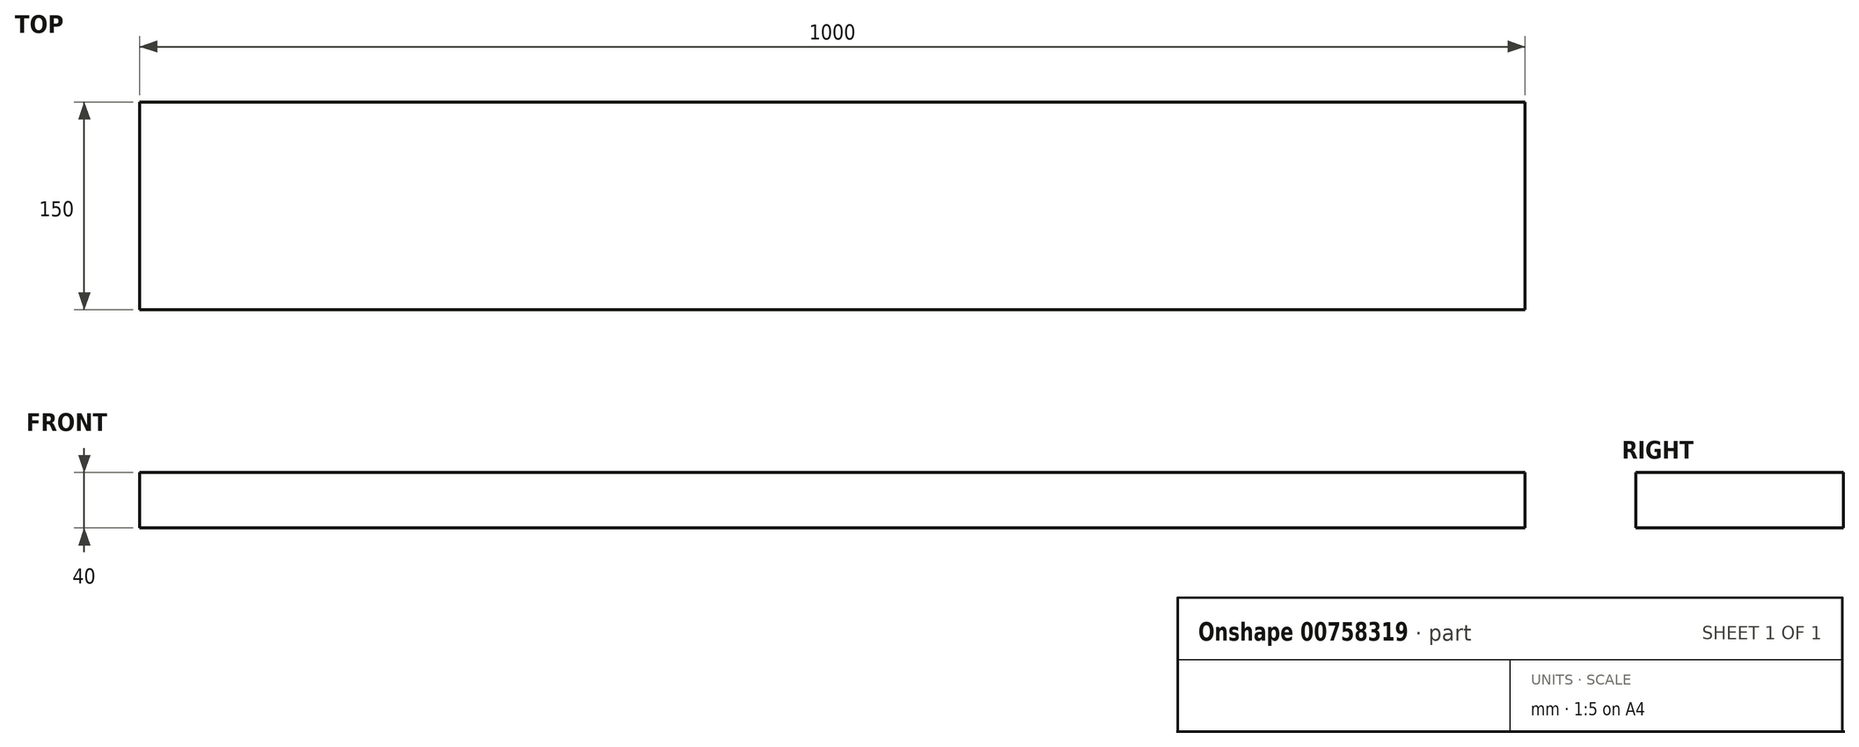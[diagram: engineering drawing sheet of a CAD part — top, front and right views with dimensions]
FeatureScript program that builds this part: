
annotation { "Feature Type Name" : "Feature", "Feature Type Description" : "" }
export const myFeature = defineFeature(function(context is Context, id is Id, definition is map)
    precondition{}
    {
        {
            var Q0;
            Q0=qCreatedBy(makeId("Top.planeOp"),FACE);
            var sketch = newSketch(context, id + "F0", { "sketchPlane" : qUnion([Q0])});
            skLineSegment(sketch, "E0.bottom", {"start": v(0, 0) * mm, "end": v(1000, 0) * mm});
            skLineSegment(sketch, "E0.top", {"start": v(0, 150) * mm, "end": v(1000, 150) * mm});
            skLineSegment(sketch, "E0.left", {"start": v(0, 0) * mm, "end": v(0, 150) * mm});
            skLineSegment(sketch, "E0.right", {"start": v(1000, 0) * mm, "end": v(1000, 150) * mm});
            skSolve(sketch);
        }
        {
            var Q0;
            Q0 = qSketchRegion(id + "F0", true);
            extrude(context, id + "F1", {"entities" : qUnion([Q0]), "depth" : 40 * mm, "offsetDistance" : 25 * mm});
        }
    });
